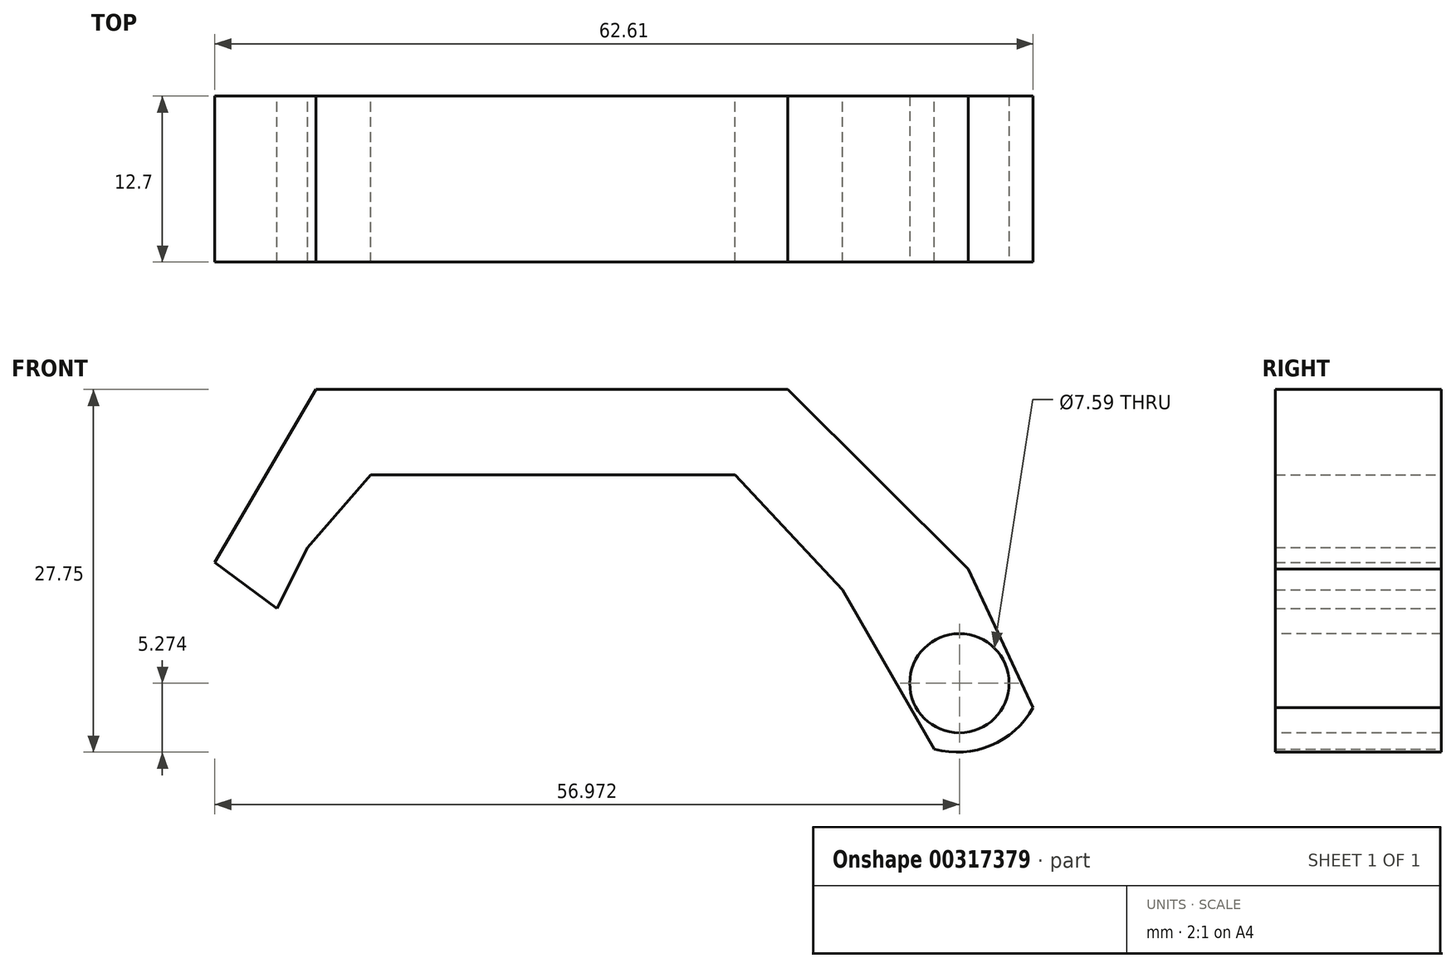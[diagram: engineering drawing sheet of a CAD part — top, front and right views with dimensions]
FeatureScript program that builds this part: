
annotation { "Feature Type Name" : "Feature", "Feature Type Description" : "" }
export const myFeature = defineFeature(function(context is Context, id is Id, definition is map)
    precondition{}
    {
        {
            var Q0;
            Q0=qCreatedBy(makeId("Front.planeOp"),FACE);
            var sketch = newSketch(context, id + "F0", { "sketchPlane" : qUnion([Q0])});
            skLineSegment(sketch, "E0", {"start": v(-24.33, 0) * mm, "end": v(3.55, 0) * mm});
            skLineSegment(sketch, "E1", {"start": v(3.55, 0) * mm, "end": v(11.76, -8.78) * mm});
            skLineSegment(sketch, "E2", {"start": v(11.76, -8.78) * mm, "end": v(18.78, -20.98) * mm});
            skLineSegment(sketch, "E3", {"start": v(-24.33, 0) * mm, "end": v(-29.17, -5.56) * mm});
            skPoint(sketch, "E4.endSnap0", {"position": v(-31.5, -7.17) * mm});
            skPoint(sketch, "E4.end.orphan", {"position": v(-31.5, -6.1) * mm});
            skPoint(sketch, "E4.start.orphan", {"position": v(-33.84, -8.78) * mm});
            skLineSegment(sketch, "E5", {"start": v(-29.17, -5.56) * mm, "end": v(-31.5, -10.23) * mm});
            skLineSegment(sketch, "E6", {"start": v(18.78, -20.98) * mm, "end": v(21.04, -25.82) * mm});
            skLineSegment(sketch, "E7", {"start": v(22.33, -25.82) * mm, "end": v(27.1, -19.45) * mm});
            skLineSegment(sketch, "E8", {"start": v(27.1, -19.45) * mm, "end": v(21.39, -7.22) * mm});
            skPoint(sketch, "E9.end.orphan", {"position": v(-29.33, -10.23) * mm});
            skLineSegment(sketch, "E10", {"start": v(21.39, -7.22) * mm, "end": v(7.57, 6.53) * mm});
            skLineSegment(sketch, "E11", {"start": v(7.57, 6.53) * mm, "end": v(-28.52, 6.53) * mm});
            skLineSegment(sketch, "E12", {"start": v(-28.52, 6.53) * mm, "end": v(-36.58, -7.22) * mm});
            skLineSegment(sketch, "E13", {"start": v(-36.27, -6.7) * mm, "end": v(-31.5, -10.23) * mm});
            skLineSegment(sketch, "E14", {"start": v(21.04, -25.82) * mm, "end": v(22.33, -25.82) * mm});
            skSolve(sketch);
        }
        {
            var Q0;
            Q0=makeQuery(id+"F0.imprint","IMPRINT",FACE,{"disambiguationData":[TD([[makeQuery(id+"F0.imprint","IMPRINT",EDGE,{"derivedFrom":sQuery(id+"F0.wireOp",EDGE,"E0")}),1.0]])]});
            extrude(context, id + "F1", {"entities" : qUnion([Q0]), "depth" : 12.7 * mm});
        }
        {
            var Q0;
            Q0=makeQuery(id+"F1.opExtrude","CAP_FACE",FACE,{"disambiguationData":[OSD([sQuery(id+"F0.wireOp",EDGE,"E0"),sQuery(id+"F0.wireOp",EDGE,"E1"),sQuery(id+"F0.wireOp",EDGE,"E2"),sQuery(id+"F0.wireOp",EDGE,"E3"),sQuery(id+"F0.wireOp",EDGE,"E5"),sQuery(id+"F0.wireOp",EDGE,"E6"),sQuery(id+"F0.wireOp",EDGE,"E7"),sQuery(id+"F0.wireOp",EDGE,"E8"),sQuery(id+"F0.wireOp",EDGE,"E10"),sQuery(id+"F0.wireOp",EDGE,"E11"),sQuery(id+"F0.wireOp",EDGE,"E12"),sQuery(id+"F0.wireOp",EDGE,"E13"),sQuery(id+"F0.wireOp",EDGE,"E14")])],"isStart":false});
            var sketch = newSketch(context, id + "F2", { "sketchPlane" : qUnion([Q0])});
            skLineSegment(sketch, "E15", {"start": v(0, 0) * mm, "end": v(20.7, -15.95) * mm, "construction": true});
            skSolve(sketch);
        }
        {
            var Q0;
            Q0=sQuery(id+"F2.wireOp",VERTEX,"E15.end");
            var Q1;
            Q1=makeQuery(id+"F1.opExtrude","SWEPT_BODY",BODY,{"disambiguationData":[OSD([sQuery(id+"F0.wireOp",EDGE,"E0"),sQuery(id+"F0.wireOp",EDGE,"E1"),sQuery(id+"F0.wireOp",EDGE,"E2"),sQuery(id+"F0.wireOp",EDGE,"E3"),sQuery(id+"F0.wireOp",EDGE,"E5"),sQuery(id+"F0.wireOp",EDGE,"E6"),sQuery(id+"F0.wireOp",EDGE,"E7"),sQuery(id+"F0.wireOp",EDGE,"E8"),sQuery(id+"F0.wireOp",EDGE,"E10"),sQuery(id+"F0.wireOp",EDGE,"E11"),sQuery(id+"F0.wireOp",EDGE,"E12"),sQuery(id+"F0.wireOp",EDGE,"E13"),sQuery(id+"F0.wireOp",EDGE,"E14")])]});
            hole(context, id + "F3", {"style" : HoleStyle.SIMPLE, "endStyle" : HoleEndStyle.THROUGH, "holeDiameter" : 7.6 * mm, "tappedDepth" : 12.7 * mm, "tapClearance" : 3, "locations" : qUnion([Q0]), "scope" : qUnion([Q1])});
        }
        {
            var Q0;
            Q0=makeQuery(id+"F1.opExtrude","CAP_FACE",FACE,{"disambiguationData":[OSD([sQuery(id+"F0.wireOp",EDGE,"E0"),sQuery(id+"F0.wireOp",EDGE,"E1"),sQuery(id+"F0.wireOp",EDGE,"E2"),sQuery(id+"F0.wireOp",EDGE,"E3"),sQuery(id+"F0.wireOp",EDGE,"E5"),sQuery(id+"F0.wireOp",EDGE,"E6"),sQuery(id+"F0.wireOp",EDGE,"E7"),sQuery(id+"F0.wireOp",EDGE,"E8"),sQuery(id+"F0.wireOp",EDGE,"E10"),sQuery(id+"F0.wireOp",EDGE,"E11"),sQuery(id+"F0.wireOp",EDGE,"E12"),sQuery(id+"F0.wireOp",EDGE,"E13"),sQuery(id+"F0.wireOp",EDGE,"E14")])],"isStart":false});
            var sketch = newSketch(context, id + "F4", { "sketchPlane" : qUnion([Q0])});
            skArc(sketch, "E16", {"start": v(18.78, -20.98) * mm, "mid": v(23.1, -20.7) * mm, "end": v(26.34, -17.82) * mm});
            skSolve(sketch);
        }
        {
            var Q0;
            {var subQ1=sQuery(id+"F4.wireOp",EDGE,"E16");Q0=makeQuery(id+"F4.imprint","IMPRINT",FACE,{"disambiguationData":[TD([[makeQuery(id+"F4.imprint","IMPRINT",EDGE,{"derivedFrom":subQ1}),-1.0]])]});}
            extrude(context, id + "F5", {"entities" : qUnion([Q0]), "operationType" : NewBodyOperationType.REMOVE, "oppositeDirection" : true, "depth" : 25.4 * mm});
        }
    });
